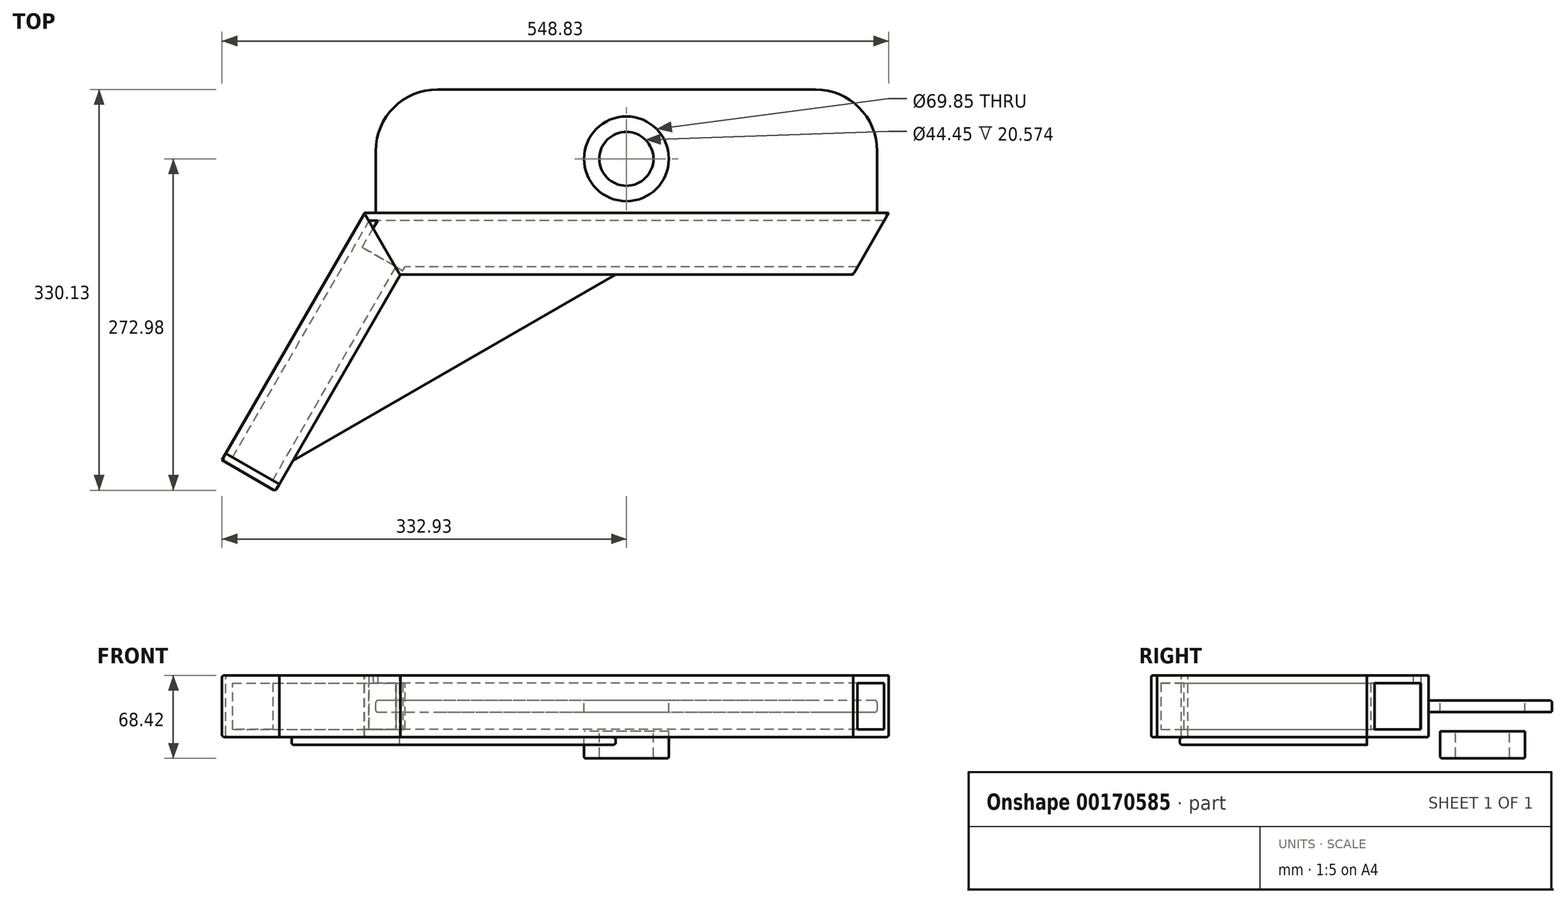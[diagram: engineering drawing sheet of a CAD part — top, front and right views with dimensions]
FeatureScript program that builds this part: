
annotation { "Feature Type Name" : "Feature", "Feature Type Description" : "" }
export const myFeature = defineFeature(function(context is Context, id is Id, definition is map)
    precondition{}
    {
        {
            var Q0;
            Q0=qCreatedBy(makeId("Right.planeOp"),FACE);
            var sketch = newSketch(context, id + "F0", { "sketchPlane" : qUnion([Q0])});
            skLineSegment(sketch, "E0.bottom", {"start": v(25.4, -25.4) * mm, "end": v(-25.4, -25.4) * mm});
            skLineSegment(sketch, "E0.top", {"start": v(25.4, 25.4) * mm, "end": v(-25.4, 25.4) * mm});
            skLineSegment(sketch, "E0.left", {"start": v(25.4, -25.4) * mm, "end": v(25.4, 25.4) * mm});
            skLineSegment(sketch, "E0.right", {"start": v(-25.4, -25.4) * mm, "end": v(-25.4, 25.4) * mm});
            skPoint(sketch, "E0.middle", {"position": v(0, 0) * mm});
            skLineSegment(sketch, "E1.0", {"start": v(19.05, 19.05) * mm, "end": v(-19.05, 19.05) * mm});
            skLineSegment(sketch, "E1.1", {"start": v(19.05, -19.05) * mm, "end": v(19.05, 19.05) * mm});
            skLineSegment(sketch, "E1.2", {"start": v(19.05, -19.05) * mm, "end": v(-19.05, -19.05) * mm});
            skLineSegment(sketch, "E1.3", {"start": v(-19.05, -19.05) * mm, "end": v(-19.05, 19.05) * mm});
            skSolve(sketch);
        }
        {
            var Q0;
            Q0=makeQuery(id+"F0.imprint","IMPRINT",FACE,{"disambiguationData":[TD([[makeQuery(id+"F0.imprint","IMPRINT",EDGE,{"derivedFrom":sQuery(id+"F0.wireOp",EDGE,"E0.bottom")}),-1.0]])]});
            extrude(context, id + "F1", {"entities" : qUnion([Q0]), "depth" : 431.8 * mm});
        }
        {
            var Q0;
            Q0=makeQuery(id+"F1.opExtrude","SWEPT_FACE",FACE,{"disambiguationData":[OSD([sQuery(id+"F0.wireOp",EDGE,"E0.top")])]});
            var sketch = newSketch(context, id + "F2", { "sketchPlane" : qUnion([Q0])});
            skLineSegment(sketch, "E2", {"start": v(0, 25.4) * mm, "end": v(29.33, -25.4) * mm});
            skLineSegment(sketch, "E3", {"start": v(431.8, 25.4) * mm, "end": v(402.47, -25.4) * mm});
            skSolve(sketch);
        }
        {
            var Q0;
            {var subQ0=sQuery(id+"F2.wireOp",EDGE,"E2");Q0=makeQuery(id+"F2.imprint","IMPRINT",FACE,{"disambiguationData":[TD([[makeQuery(id+"F2.imprint","IMPRINT",EDGE,{"derivedFrom":subQ0}),-1.0]])]});}
            var Q1;
            {var subQ0=sQuery(id+"F2.wireOp",EDGE,"E3");Q1=makeQuery(id+"F2.imprint","IMPRINT",FACE,{"disambiguationData":[TD([[makeQuery(id+"F2.imprint","IMPRINT",EDGE,{"derivedFrom":subQ0}),1.0]])]});}
            extrude(context, id + "F3", {"entities" : qUnion([Q0, Q1]), "operationType" : NewBodyOperationType.REMOVE, "endBound" : BoundingType.THROUGH_ALL, "oppositeDirection" : true, "depth" : 25.4 * mm});
        }
        {
            var Q0;
            Q0=makeQuery(id+"F1.opExtrude","SWEPT_FACE",FACE,{"disambiguationData":[OSD([sQuery(id+"F0.wireOp",EDGE,"E0.bottom")])]});
            var sketch = newSketch(context, id + "F4", { "sketchPlane" : qUnion([Q0])});
            skLineSegment(sketch, "E4", {"start": v(0, -25.4) * mm, "end": v(-95.34, 139.74) * mm});
            skLineSegment(sketch, "E5", {"start": v(0, -25.4) * mm, "end": v(150.46, 61.47) * mm});
            skSolve(sketch);
        }
        {
            var Q0;
            Q0=qCreatedBy(makeId("Right.planeOp"),FACE);
            var Q1;
            Q1=sQuery(id+"F4.wireOp",EDGE,"E5");
            cPlane(context, id + "F5", {"entities" : qUnion([Q0, Q1]), "cplaneType" : CPlaneType.LINE_ANGLE, "offset" : 25.4 * mm, "angle" : 0 * degree, "width" : 152.4 * mm, "height" : 152.4 * mm});
        }
        {
            var Q0;
            Q0=qCreatedBy(id+"F5.planeOp",FACE);
            var sketch = newSketch(context, id + "F6", { "sketchPlane" : qUnion([Q0])});
            skLineSegment(sketch, "E6", {"start": v(-12.18, -25.24) * mm, "end": v(-12.18, 25.56) * mm});
            skLineSegment(sketch, "E7", {"start": v(-12.18, 25.56) * mm, "end": v(38.62, 25.56) * mm});
            skLineSegment(sketch, "E8", {"start": v(38.62, 25.56) * mm, "end": v(38.62, -25.24) * mm});
            skLineSegment(sketch, "E9", {"start": v(38.62, -25.24) * mm, "end": v(-12.18, -25.24) * mm});
            skLineSegment(sketch, "E10.0", {"start": v(-5.83, -18.89) * mm, "end": v(-5.83, 19.21) * mm});
            skLineSegment(sketch, "E10.1", {"start": v(32.27, -18.89) * mm, "end": v(-5.83, -18.89) * mm});
            skLineSegment(sketch, "E10.2", {"start": v(32.27, 19.21) * mm, "end": v(32.27, -18.89) * mm});
            skLineSegment(sketch, "E10.3", {"start": v(-5.83, 19.21) * mm, "end": v(32.27, 19.21) * mm});
            skSolve(sketch);
        }
        {
            var Q0;
            Q0=makeQuery(id+"F6.imprint","IMPRINT",FACE,{"disambiguationData":[TD([[makeQuery(id+"F6.imprint","IMPRINT",EDGE,{"derivedFrom":sQuery(id+"F6.wireOp",EDGE,"E6")}),-1.0]])]});
            extrude(context, id + "F7", {"entities" : qUnion([Q0]), "depth" : 228.6 * mm});
        }
        {
            var Q0;
            Q0=makeQuery(id+"F1.opExtrude","SWEPT_BODY",BODY,{"disambiguationData":[OSD([sQuery(id+"F0.wireOp",EDGE,"E0.bottom"),sQuery(id+"F0.wireOp",EDGE,"E0.top"),sQuery(id+"F0.wireOp",EDGE,"E0.left"),sQuery(id+"F0.wireOp",EDGE,"E0.right"),sQuery(id+"F0.wireOp",EDGE,"E1.0"),sQuery(id+"F0.wireOp",EDGE,"E1.1"),sQuery(id+"F0.wireOp",EDGE,"E1.2"),sQuery(id+"F0.wireOp",EDGE,"E1.3")])]});
            var Q1;
            Q1=makeQuery(id+"F7.opExtrude","SWEPT_BODY",BODY,{"disambiguationData":[OSD([sQuery(id+"F6.wireOp",EDGE,"E6"),sQuery(id+"F6.wireOp",EDGE,"E7"),sQuery(id+"F6.wireOp",EDGE,"E8"),sQuery(id+"F6.wireOp",EDGE,"E9"),sQuery(id+"F6.wireOp",EDGE,"E10.0"),sQuery(id+"F6.wireOp",EDGE,"E10.1"),sQuery(id+"F6.wireOp",EDGE,"E10.2"),sQuery(id+"F6.wireOp",EDGE,"E10.3")])]});
            booleanBodies(context, id + "F8", {"operationType" : BooleanOperationType.SUBTRACTION, "tools" : qUnion([Q0]), "targets" : qUnion([Q1]), "keepTools" : true});
        }
        {
            var Q0;
            Q0=makeQuery(id+"F8.opBoolean","COPY",FACE,{"derivedFrom":makeQuery(id+"F1.opExtrude","SWEPT_FACE",FACE,{"disambiguationData":[OSD([sQuery(id+"F0.wireOp",EDGE,"E0.top")])]})});
            extrude(context, id + "F9", {"entities" : qUnion([Q0]), "operationType" : NewBodyOperationType.REMOVE, "oppositeDirection" : true, "depth" : 25.4 * mm});
        }
        {
            var Q0;
            {var subQ0=sQuery(id+"F6.wireOp",EDGE,"E8");var subQ1=sQuery(id+"F6.wireOp",EDGE,"E10.1");var subQ2=sQuery(id+"F6.wireOp",EDGE,"E10.2");Q0=makeQuery(id+"F8.opBoolean","SPLIT",FACE,{"disambiguationData":[TD([makeQuery(id+"F1.opExtrude","SWEPT_FACE",FACE,{"disambiguationData":[OSD([sQuery(id+"F0.wireOp",EDGE,"E1.0")])]})])],"derivedFrom":makeQuery(id+"F7.opExtrude","CAP_FACE",FACE,{"disambiguationData":[OSD([sQuery(id+"F6.wireOp",EDGE,"E6"),sQuery(id+"F6.wireOp",EDGE,"E7"),subQ0,sQuery(id+"F6.wireOp",EDGE,"E9"),sQuery(id+"F6.wireOp",EDGE,"E10.0"),subQ1,subQ2,sQuery(id+"F6.wireOp",EDGE,"E10.3")])],"isStart":true})});}
            extrude(context, id + "F10", {"entities" : qUnion([Q0]), "operationType" : NewBodyOperationType.REMOVE, "oppositeDirection" : true, "depth" : 25.4 * mm});
        }
        {
            var Q0;
            {var subQ1=sQuery(id+"F0.wireOp",EDGE,"E1.1");var subQ10=sQuery(id+"F0.wireOp",EDGE,"E1.2");Q0=makeQuery(id+"F10.boolean.opBoolean","SPLIT",FACE,{"disambiguationData":[TD([makeQuery(id+"F8.opBoolean","COPY",FACE,{"derivedFrom":makeQuery(id+"F1.opExtrude","SWEPT_FACE",FACE,{"disambiguationData":[OSD([subQ1])]})})])],"derivedFrom":makeQuery(id+"F8.opBoolean","COPY",FACE,{"derivedFrom":makeQuery(id+"F1.opExtrude","SWEPT_FACE",FACE,{"disambiguationData":[OSD([subQ10])]})})});}
            extrude(context, id + "F11", {"entities" : qUnion([Q0]), "operationType" : NewBodyOperationType.REMOVE, "endBound" : BoundingType.THROUGH_ALL, "oppositeDirection" : true, "depth" : 25.4 * mm});
        }
        {
            var Q0;
            Q0=makeQuery(id+"F1.opExtrude","SWEPT_FACE",FACE,{"disambiguationData":[OSD([sQuery(id+"F0.wireOp",EDGE,"E0.left")])]});
            var sketch = newSketch(context, id + "F12", { "sketchPlane" : qUnion([Q0])});
            skLineSegment(sketch, "E11", {"start": v(-422.28, 4.76) * mm, "end": v(-9.53, 4.76) * mm});
            skLineSegment(sketch, "E12", {"start": v(-9.53, -4.76) * mm, "end": v(-422.28, -4.76) * mm});
            skLineSegment(sketch, "E13", {"start": v(-422.28, 4.76) * mm, "end": v(-422.28, -4.76) * mm});
            skLineSegment(sketch, "E14", {"start": v(-9.53, -4.76) * mm, "end": v(-9.53, 4.76) * mm});
            skSolve(sketch);
        }
        {
            var Q0;
            Q0=makeQuery(id+"F12.imprint","IMPRINT",FACE,{"disambiguationData":[TD([[makeQuery(id+"F12.imprint","IMPRINT",EDGE,{"derivedFrom":sQuery(id+"F12.wireOp",EDGE,"E11")}),-1.0]])]});
            extrude(context, id + "F13", {"entities" : qUnion([Q0]), "depth" : 101.6 * mm});
        }
        {
            var Q0;
            Q0=makeQuery(id+"F13.opExtrude","CAP_EDGE",EDGE,{"disambiguationData":[OSD([sQuery(id+"F12.wireOp",EDGE,"E14")])],"isStart":false});
            var Q1;
            Q1=makeQuery(id+"F13.opExtrude","CAP_EDGE",EDGE,{"disambiguationData":[OSD([sQuery(id+"F12.wireOp",EDGE,"E13")])],"isStart":false});
            fillet(context, id + "F14", {"entities" : qUnion([Q0, Q1]), "radius" : 50.8 * mm, "tangentPropagation" : true, "allowEdgeOverflow" : false});
        }
        {
            var Q0;
            Q0=makeQuery(id+"F13.opExtrude","SWEPT_FACE",FACE,{"disambiguationData":[OSD([sQuery(id+"F12.wireOp",EDGE,"E12")])]});
            var sketch = newSketch(context, id + "F15", { "sketchPlane" : qUnion([Q0])});
            skCircle(sketch, "E15", {"center": v(215.9, -69.85) * mm, "radius": 34.93 * mm});
            skCircle(sketch, "E16", {"center": v(215.9, -69.85) * mm, "radius": 22.23 * mm});
            skSolve(sketch);
        }
        {
            var Q0;
            Q0=makeQuery(id+"F15.imprint","IMPRINT",FACE,{"disambiguationData":[TD([[makeQuery(id+"F15.imprint","IMPRINT",EDGE,{"derivedFrom":sQuery(id+"F15.wireOp",EDGE,"E16")}),1.0]])]});
            extrude(context, id + "F16", {"entities" : qUnion([Q0]), "operationType" : NewBodyOperationType.REMOVE, "oppositeDirection" : true, "depth" : 25.4 * mm});
        }
        {
            var Q0;
            Q0 = qSketchRegion(id + "F15", true);
            extrude(context, id + "F17", {"entities" : qUnion([Q0]), "depth" : 38.1 * mm});
        }
        {
            var Q0;
            Q0=makeQuery(id+"F17.opExtrude","SWEPT_BODY",BODY,{"disambiguationData":[OSD([sQuery(id+"F15.wireOp",EDGE,"E15"),sQuery(id+"F15.wireOp",EDGE,"E16")])]});
            var Q1;
            Q1=makeQuery(id+"F13.opExtrude","SWEPT_BODY",BODY,{"disambiguationData":[OSD([sQuery(id+"F12.wireOp",EDGE,"E11"),sQuery(id+"F12.wireOp",EDGE,"E12"),sQuery(id+"F12.wireOp",EDGE,"E13"),sQuery(id+"F12.wireOp",EDGE,"E14")])]});
            booleanBodies(context, id + "F18", {"operationType" : BooleanOperationType.SUBTRACTION, "tools" : qUnion([Q0]), "targets" : qUnion([Q1]), "keepTools" : true});
        }
        {
            var Q0;
            Q0=makeQuery(id+"F7.opExtrude","CAP_FACE",FACE,{"disambiguationData":[OSD([sQuery(id+"F6.wireOp",EDGE,"E6"),sQuery(id+"F6.wireOp",EDGE,"E7"),sQuery(id+"F6.wireOp",EDGE,"E8"),sQuery(id+"F6.wireOp",EDGE,"E9"),sQuery(id+"F6.wireOp",EDGE,"E10.0"),sQuery(id+"F6.wireOp",EDGE,"E10.1"),sQuery(id+"F6.wireOp",EDGE,"E10.2"),sQuery(id+"F6.wireOp",EDGE,"E10.3")])],"isStart":false});
            var sketch = newSketch(context, id + "F19", { "sketchPlane" : qUnion([Q0])});
            skLineSegment(sketch, "E17.bottom", {"start": v(38.62, -25.24) * mm, "end": v(-12.18, -25.24) * mm});
            skLineSegment(sketch, "E17.top", {"start": v(38.62, 25.56) * mm, "end": v(-12.18, 25.56) * mm});
            skLineSegment(sketch, "E17.left", {"start": v(38.62, -25.24) * mm, "end": v(38.62, 25.56) * mm});
            skLineSegment(sketch, "E17.right", {"start": v(-12.18, -25.24) * mm, "end": v(-12.18, 25.56) * mm});
            skSolve(sketch);
        }
        {
            var Q0;
            Q0=makeQuery(id+"F19.imprint","IMPRINT",FACE,{"disambiguationData":[TD([[makeQuery(id+"F19.imprint","IMPRINT",EDGE,{"derivedFrom":makeQuery(id+"F7.opExtrude","CAP_EDGE",EDGE,{"disambiguationData":[OSD([sQuery(id+"F6.wireOp",EDGE,"E10.0")])],"isStart":false})}),-1.0]])]});
            var Q1;
            Q1=makeQuery(id+"F19.imprint","IMPRINT",FACE,{"disambiguationData":[TD([[makeQuery(id+"F19.imprint","IMPRINT",EDGE,{"derivedFrom":sQuery(id+"F19.wireOp",EDGE,"E17.bottom")}),-1.0]])]});
            extrude(context, id + "F20", {"entities" : qUnion([Q0, Q1]), "depth" : 6.35 * mm});
        }
        {
            var Q0;
            Q0=makeQuery(id+"F1.opExtrude","SWEPT_FACE",FACE,{"disambiguationData":[OSD([sQuery(id+"F0.wireOp",EDGE,"E0.bottom")])]});
            var sketch = newSketch(context, id + "F21", { "sketchPlane" : qUnion([Q0])});
            skLineSegment(sketch, "E18", {"start": v(29.33, 25.4) * mm, "end": v(-59.6, 179.36) * mm});
            skLineSegment(sketch, "E19", {"start": v(-59.6, 179.36) * mm, "end": v(207.13, 25.4) * mm});
            skLineSegment(sketch, "E20", {"start": v(207.13, 25.4) * mm, "end": v(29.33, 25.4) * mm});
            skSolve(sketch);
        }
        {
            var Q0;
            Q0=makeQuery(id+"F21.imprint","IMPRINT",FACE,{"disambiguationData":[TD([[makeQuery(id+"F21.imprint","IMPRINT",EDGE,{"derivedFrom":sQuery(id+"F21.wireOp",EDGE,"E18")}),-1.0]])]});
            extrude(context, id + "F22", {"entities" : qUnion([Q0]), "depth" : 6.35 * mm});
        }
        {
            var Q0;
            Q0=makeQuery(id+"F7.opExtrude","SWEPT_EDGE",EDGE,{"disambiguationData":[OSD([sQuery(id+"F6.wireOp",EDGE,"E7"),sQuery(id+"F6.wireOp",EDGE,"E8")])]});
            var Q1;
            Q1=makeQuery(id+"F22.opExtrude","CAP_EDGE",EDGE,{"disambiguationData":[OSD([sQuery(id+"F21.wireOp",EDGE,"E19")])],"isStart":true});
            var Q2;
            Q2=makeQuery(id+"F22.opExtrude","CAP_EDGE",EDGE,{"disambiguationData":[OSD([sQuery(id+"F21.wireOp",EDGE,"E19")])],"isStart":false});
            var Q3;
            Q3=makeQuery(id+"F7.opExtrude","SWEPT_EDGE",EDGE,{"disambiguationData":[OSD([sQuery(id+"F6.wireOp",EDGE,"E8"),sQuery(id+"F6.wireOp",EDGE,"E9")])]});
            var Q4;
            Q4=makeQuery(id+"F7.opExtrude","SWEPT_EDGE",EDGE,{"disambiguationData":[OSD([sQuery(id+"F6.wireOp",EDGE,"E6"),sQuery(id+"F6.wireOp",EDGE,"E7")])]});
            var Q5;
            Q5=makeQuery(id+"F20.opExtrude","CAP_EDGE",EDGE,{"disambiguationData":[OSD([sQuery(id+"F19.wireOp",EDGE,"E17.top")])],"isStart":false});
            var Q6;
            Q6=makeQuery(id+"F20.opExtrude","SWEPT_EDGE",EDGE,{"disambiguationData":[OSD([sQuery(id+"F19.wireOp",EDGE,"E17.top"),sQuery(id+"F19.wireOp",EDGE,"E17.left")])]});
            var Q7;
            Q7=makeQuery(id+"F20.opExtrude","SWEPT_EDGE",EDGE,{"disambiguationData":[OSD([sQuery(id+"F19.wireOp",EDGE,"E17.bottom"),sQuery(id+"F19.wireOp",EDGE,"E17.left")])]});
            var Q8;
            Q8=makeQuery(id+"F20.opExtrude","CAP_EDGE",EDGE,{"disambiguationData":[OSD([sQuery(id+"F19.wireOp",EDGE,"E17.left")])],"isStart":false});
            var Q9;
            Q9=makeQuery(id+"F20.opExtrude","CAP_EDGE",EDGE,{"disambiguationData":[OSD([sQuery(id+"F19.wireOp",EDGE,"E17.bottom")])],"isStart":false});
            var Q10;
            Q10=makeQuery(id+"F1.opExtrude","SWEPT_EDGE",EDGE,{"disambiguationData":[OSD([sQuery(id+"F0.wireOp",EDGE,"E0.bottom"),sQuery(id+"F0.wireOp",EDGE,"E0.right")])]});
            var Q11;
            Q11=makeQuery(id+"F1.opExtrude","SWEPT_EDGE",EDGE,{"disambiguationData":[OSD([sQuery(id+"F0.wireOp",EDGE,"E0.top"),sQuery(id+"F0.wireOp",EDGE,"E0.right")])]});
            var Q12;
            Q12=makeQuery(id+"F3.boolean.opBoolean","COPY",EDGE,{"derivedFrom":makeQuery(id+"F3.opExtrude","SWEPT_EDGE",EDGE,{"disambiguationData":[OSD([sQuery(id+"F0.wireOp",EDGE,"E0.top"),sQuery(id+"F0.wireOp",EDGE,"E0.right"),sQuery(id+"F2.wireOp",EDGE,"E3")])]})});
            var Q13;
            Q13=makeQuery(id+"F3.boolean.opBoolean","COPY",EDGE,{"derivedFrom":makeQuery(id+"F3.opExtrude","CAP_EDGE",EDGE,{"disambiguationData":[OSD([sQuery(id+"F2.wireOp",EDGE,"E3")])],"isStart":true})});
            var Q14;
            Q14=makeQuery(id+"F3.boolean.opBoolean","INTERSECT",EDGE,{"derivedFrom":[makeQuery(id+"F1.opExtrude","SWEPT_FACE",FACE,{"disambiguationData":[OSD([sQuery(id+"F0.wireOp",EDGE,"E0.bottom")])]}),makeQuery(id+"F3.opExtrude","SWEPT_FACE",FACE,{"disambiguationData":[OSD([sQuery(id+"F2.wireOp",EDGE,"E3")])]})]});
            var Q15;
            Q15=makeQuery(id+"F7.opExtrude","SWEPT_EDGE",EDGE,{"disambiguationData":[OSD([sQuery(id+"F6.wireOp",EDGE,"E6"),sQuery(id+"F6.wireOp",EDGE,"E9")])]});
            var Q16;
            Q16=makeQuery(id+"F20.opExtrude","SWEPT_EDGE",EDGE,{"disambiguationData":[OSD([sQuery(id+"F19.wireOp",EDGE,"E17.bottom"),sQuery(id+"F19.wireOp",EDGE,"E17.right")])]});
            var Q17;
            Q17=makeQuery(id+"F20.opExtrude","SWEPT_EDGE",EDGE,{"disambiguationData":[OSD([sQuery(id+"F19.wireOp",EDGE,"E17.top"),sQuery(id+"F19.wireOp",EDGE,"E17.right")])]});
            var Q18;
            Q18=makeQuery(id+"F1.opExtrude","SWEPT_EDGE",EDGE,{"disambiguationData":[OSD([sQuery(id+"F0.wireOp",EDGE,"E0.bottom"),sQuery(id+"F0.wireOp",EDGE,"E0.left")])]});
            var Q19;
            Q19=makeQuery(id+"F13.opExtrude","SWEPT_EDGE",EDGE,{"disambiguationData":[OSD([sQuery(id+"F12.wireOp",EDGE,"E12"),sQuery(id+"F12.wireOp",EDGE,"E14")])]});
            var Q20;
            Q20=makeQuery(id+"F14.opFillet","BLEND_EDGE",EDGE,{"blendedFrom":[makeQuery(id+"F13.opExtrude","CAP_EDGE",EDGE,{"disambiguationData":[OSD([sQuery(id+"F12.wireOp",EDGE,"E14")])],"isStart":false}),makeQuery(id+"F13.opExtrude","SWEPT_FACE",FACE,{"disambiguationData":[OSD([sQuery(id+"F12.wireOp",EDGE,"E12")])]})],"blendedInto":[makeQuery(id+"F13.opExtrude","SWEPT_FACE",FACE,{"disambiguationData":[OSD([sQuery(id+"F12.wireOp",EDGE,"E12")])]})]});
            var Q21;
            Q21=makeQuery(id+"F13.opExtrude","CAP_EDGE",EDGE,{"disambiguationData":[OSD([sQuery(id+"F12.wireOp",EDGE,"E11")])],"isStart":false});
            var Q22;
            Q22=makeQuery(id+"F17.opExtrude","CAP_EDGE",EDGE,{"disambiguationData":[OSD([sQuery(id+"F15.wireOp",EDGE,"E15")])],"isStart":true});
            var Q23;
            Q23=makeQuery(id+"F17.opExtrude","CAP_EDGE",EDGE,{"disambiguationData":[OSD([sQuery(id+"F15.wireOp",EDGE,"E16")])],"isStart":true});
            var Q24;
            Q24=makeQuery(id+"F17.opExtrude","CAP_EDGE",EDGE,{"disambiguationData":[OSD([sQuery(id+"F15.wireOp",EDGE,"E15")])],"isStart":false});
            var Q25;
            Q25=makeQuery(id+"F17.opExtrude","CAP_EDGE",EDGE,{"disambiguationData":[OSD([sQuery(id+"F15.wireOp",EDGE,"E16")])],"isStart":false});
            fillet(context, id + "F23", {"entities" : qUnion([Q0, Q1, Q2, Q3, Q4, Q5, Q6, Q7, Q8, Q9, Q10, Q11, Q12, Q13, Q14, Q15, Q16, Q17, Q18, Q19, Q20, Q21, Q22, Q23, Q24, Q25]), "radius" : 1.65 * mm, "tangentPropagation" : true, "allowEdgeOverflow" : false});
        }
        {
            var Q0;
            Q0=makeQuery(id+"F13.opExtrude","SWEPT_FACE",FACE,{"disambiguationData":[OSD([sQuery(id+"F12.wireOp",EDGE,"E11")])]});
            var sketch = newSketch(context, id + "F24", { "sketchPlane" : qUnion([Q0])});
            skCircle(sketch, "E21", {"center": v(215.9, 69.85) * mm, "radius": 34.93 * mm});
            skSolve(sketch);
        }
        {
            var Q0;
            Q0=makeQuery(id+"F24.imprint","IMPRINT",FACE,{"disambiguationData":[TD([[makeQuery(id+"F24.imprint","IMPRINT",EDGE,{"derivedFrom":sQuery(id+"F24.wireOp",EDGE,"E21")}),1.0]])]});
            extrude(context, id + "F25", {"entities" : qUnion([Q0]), "operationType" : NewBodyOperationType.REMOVE, "oppositeDirection" : true, "depth" : 25.4 * mm});
        }
    });
